# Revit family: Cloakroom Ribbed 420mm WH White Cabinet & Comfort Cloakroom Vanity Basin 1th
name_source: partatom
category: Casework
units: mm (PartAtom-declared; Revit-internal decimal feet)

## family parameters
Always vertical = Yes
Cut with Voids When Loaded = No
OmniClass Number = 23.40.35.00
OmniClass Title = Casework
Room Calculation Point = No
Shared = No
Work Plane-Based = No

## types (1)
- Cloakroom Ribbed 420mm WH White Cabinet & Comfort Cloakroom Vanity Basin 1th
    Cabinet = White Melamine
    Carcass = White Melamine
    Category = Cabinets
    Colour = White
    Default Elevation = 0 mm  [stored 0 ft]
    Depth = 236 mm
    Height = 495 mm  [stored 1.62402 ft]
    Manufacturer = Lecico SA
    Material = MDF with smooth white duco oven baked finsh + Vitreous China
    Model = Cloakroom Ribbed 420mm WH White Cabinet & Comfort Cloakroom Vanity Basin 1th
    Product Code = CABDUOCOMWHITBS
    Technical Dimensions = W429 x H555 x D236mm
    URL = https://www.lecicosa.co.za
    Width = 429 mm  [stored 1.40748 ft]

note: [stored X ft] marks values corroborated as IEEE doubles in the binary element streams (Revit-internal decimal feet)

## geometry (parser evidence)
native form markers: Sweep x3
no freeform markers — native parametric forms only
